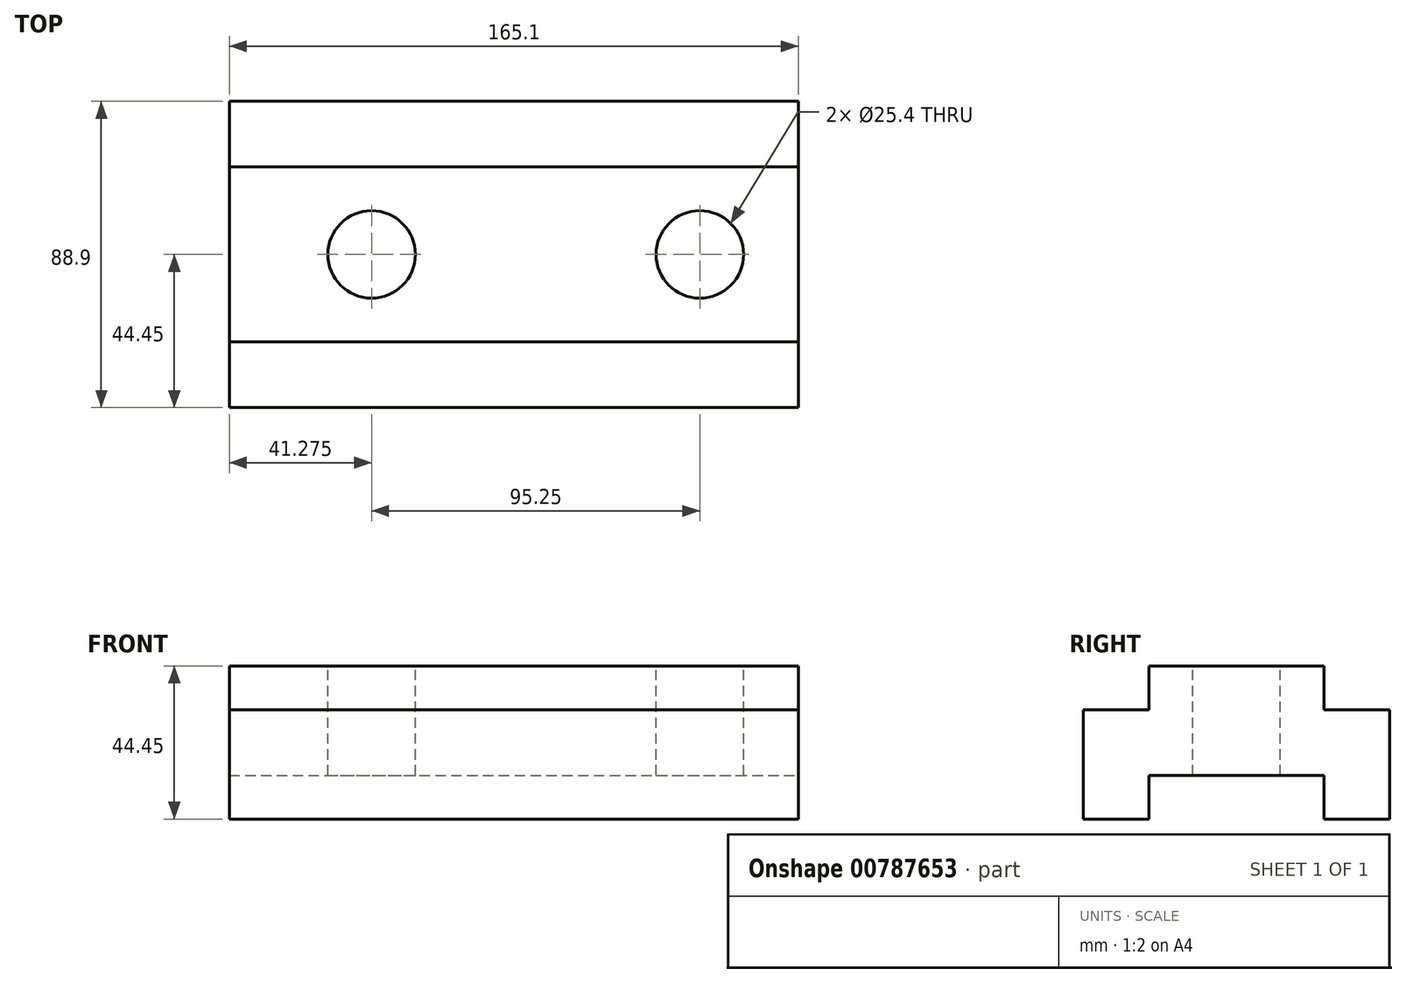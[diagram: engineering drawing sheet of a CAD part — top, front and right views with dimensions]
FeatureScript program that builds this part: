
annotation { "Feature Type Name" : "Feature", "Feature Type Description" : "" }
export const myFeature = defineFeature(function(context is Context, id is Id, definition is map)
    precondition{}
    {
        {
            var Q0;
            Q0=qCreatedBy(makeId("Right.planeOp"),FACE);
            var sketch = newSketch(context, id + "F0", { "sketchPlane" : qUnion([Q0])});
            skLineSegment(sketch, "E0", {"start": v(0, 0) * mm, "end": v(19.05, 0) * mm});
            skLineSegment(sketch, "E1", {"start": v(19.05, 0) * mm, "end": v(19.05, 12.7) * mm});
            skLineSegment(sketch, "E2", {"start": v(19.05, 12.7) * mm, "end": v(69.85, 12.7) * mm});
            skLineSegment(sketch, "E3", {"start": v(69.85, 12.7) * mm, "end": v(69.85, 0) * mm});
            skLineSegment(sketch, "E4", {"start": v(69.85, 0) * mm, "end": v(88.9, 0) * mm});
            skLineSegment(sketch, "E5", {"start": v(88.9, 0) * mm, "end": v(88.9, 31.75) * mm});
            skLineSegment(sketch, "E6", {"start": v(88.9, 31.75) * mm, "end": v(69.85, 31.75) * mm});
            skLineSegment(sketch, "E7", {"start": v(69.85, 31.75) * mm, "end": v(69.85, 44.45) * mm});
            skLineSegment(sketch, "E8", {"start": v(69.85, 44.45) * mm, "end": v(19.05, 44.45) * mm});
            skLineSegment(sketch, "E9", {"start": v(19.05, 44.45) * mm, "end": v(19.05, 31.75) * mm});
            skLineSegment(sketch, "E10", {"start": v(19.05, 31.75) * mm, "end": v(0, 31.75) * mm});
            skLineSegment(sketch, "E11", {"start": v(0, 31.75) * mm, "end": v(0, 0) * mm});
            skSolve(sketch);
        }
        {
            var Q0;
            Q0=makeQuery(id+"F0.imprint","IMPRINT",FACE,{"disambiguationData":[TD([[makeQuery(id+"F0.imprint","IMPRINT",EDGE,{"derivedFrom":sQuery(id+"F0.wireOp",EDGE,"E0")}),1.0]])]});
            extrude(context, id + "F1", {"entities" : qUnion([Q0]), "oppositeDirection" : true, "depth" : 165.1 * mm, "offsetDistance" : 25.4 * mm});
        }
        {
            var Q0;
            Q0=makeQuery(id+"F1.opExtrude","SWEPT_FACE",FACE,{"disambiguationData":[OSD([sQuery(id+"F0.wireOp",EDGE,"E8")])]});
            var sketch = newSketch(context, id + "F2", { "sketchPlane" : qUnion([Q0])});
            skLineSegment(sketch, "E12", {"start": v(-165.1, 44.45) * mm, "end": v(-123.82, 44.45) * mm, "construction": true});
            skLineSegment(sketch, "E13", {"start": v(-123.82, 44.45) * mm, "end": v(-28.58, 44.45) * mm, "construction": true});
            skCircle(sketch, "E14", {"center": v(-123.82, 44.45) * mm, "radius": 12.7 * mm, "construction": true});
            skCircle(sketch, "E15", {"center": v(-28.58, 44.45) * mm, "radius": 12.7 * mm, "construction": true});
            skCircle(sketch, "E16", {"center": v(-123.82, 44.45) * mm, "radius": 12.7 * mm});
            skCircle(sketch, "E17", {"center": v(-28.58, 44.45) * mm, "radius": 12.7 * mm});
            skSolve(sketch);
        }
        {
            var Q0;
            Q0 = qSketchRegion(id + "F2", true);
            extrude(context, id + "F3", {"entities" : qUnion([Q0]), "operationType" : NewBodyOperationType.REMOVE, "endBound" : BoundingType.THROUGH_ALL, "oppositeDirection" : true, "depth" : 25.4 * mm, "offsetDistance" : 25.4 * mm});
        }
    });
